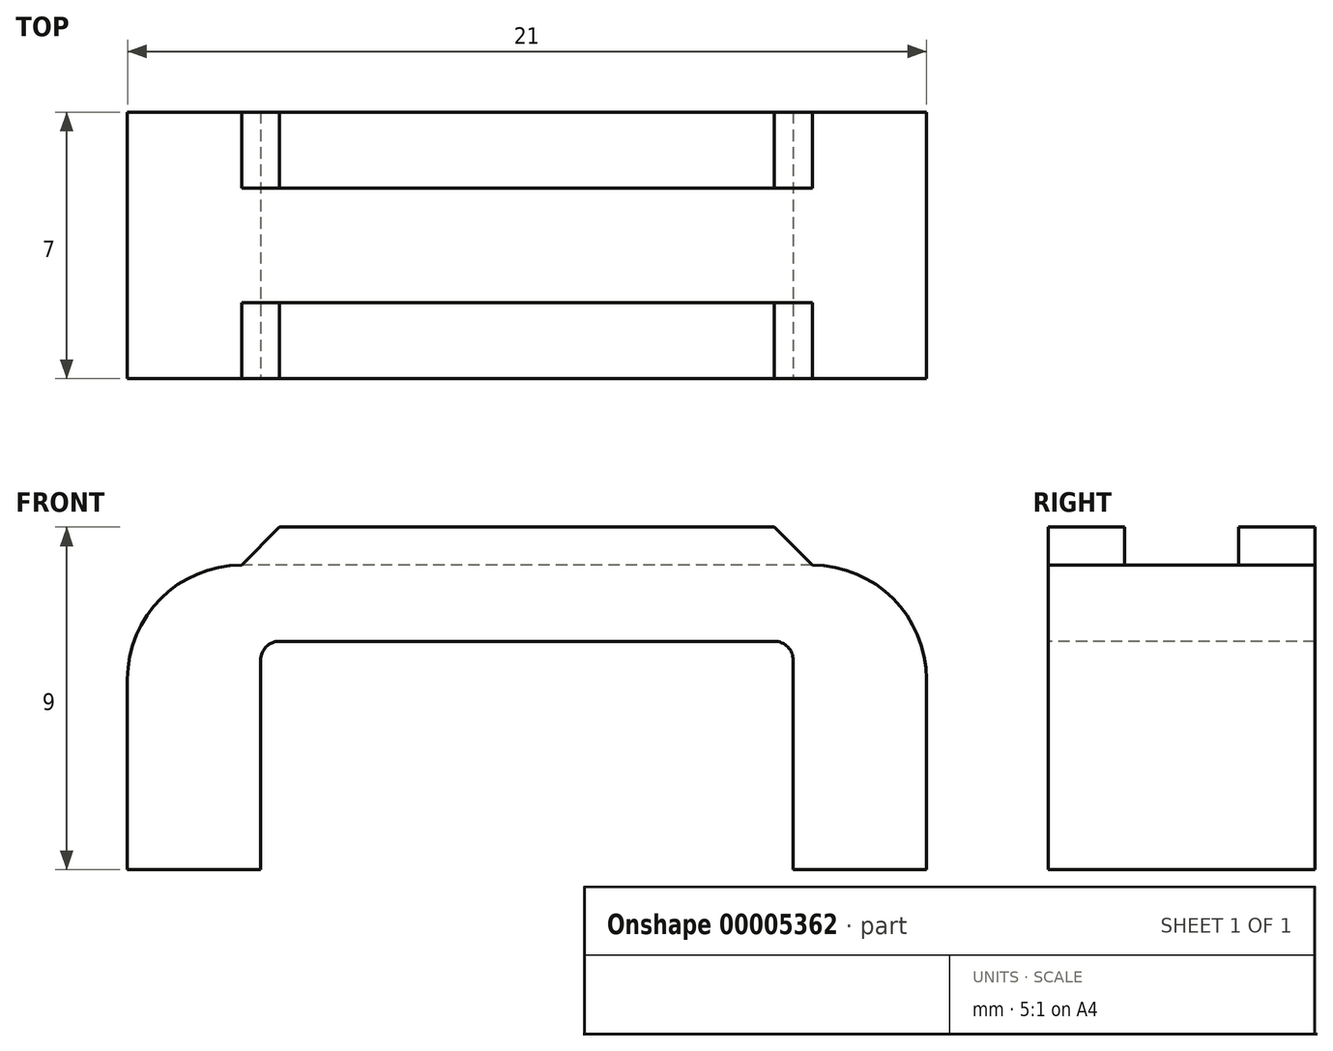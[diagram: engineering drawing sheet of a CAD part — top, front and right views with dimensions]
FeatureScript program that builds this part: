
annotation { "Feature Type Name" : "Feature", "Feature Type Description" : "" }
export const myFeature = defineFeature(function(context is Context, id is Id, definition is map)
    precondition{}
    {
        {
            var Q0;
            Q0=qCreatedBy(makeId("Top.planeOp"),FACE);
            var sketch = newSketch(context, id + "F0", { "sketchPlane" : qUnion([Q0])});
            skLineSegment(sketch, "E0.bottom", {"start": v(-26.45, 12.14) * mm, "end": v(-5.45, 12.14) * mm});
            skLineSegment(sketch, "E0.top", {"start": v(-26.45, 5.14) * mm, "end": v(-5.45, 5.14) * mm});
            skLineSegment(sketch, "E0.left", {"start": v(-26.45, 12.14) * mm, "end": v(-26.45, 5.14) * mm});
            skLineSegment(sketch, "E0.right", {"start": v(-5.45, 12.14) * mm, "end": v(-5.45, 5.14) * mm});
            skSolve(sketch);
        }
        {
            var Q0;
            Q0 = qSketchRegion(id + "F0", true);
            extrude(context, id + "F1", {"entities" : qUnion([Q0]), "depth" : 8 * mm});
        }
        {
            var Q0;
            Q0=makeQuery(id+"F1.opExtrude","SWEPT_FACE",FACE,{"disambiguationData":[OSD([sQuery(id+"F0.wireOp",EDGE,"E0.top")])]});
            var sketch = newSketch(context, id + "F2", { "sketchPlane" : qUnion([Q0])});
            skLineSegment(sketch, "E1.bottom", {"start": v(-22.95, 0) * mm, "end": v(-8.95, 0) * mm});
            skLineSegment(sketch, "E1.top", {"start": v(-22.95, 6) * mm, "end": v(-8.95, 6) * mm});
            skLineSegment(sketch, "E1.left", {"start": v(-22.95, 0) * mm, "end": v(-22.95, 6) * mm});
            skLineSegment(sketch, "E1.right", {"start": v(-8.95, 0) * mm, "end": v(-8.95, 6) * mm});
            skSolve(sketch);
        }
        {
            var Q0;
            Q0=makeQuery(id+"F2.imprint","IMPRINT",FACE,{"disambiguationData":[TD([[makeQuery(id+"F2.imprint","IMPRINT",EDGE,{"derivedFrom":sQuery(id+"F2.wireOp",EDGE,"E1.bottom")}),1.0]])]});
            extrude(context, id + "F3", {"entities" : qUnion([Q0]), "operationType" : NewBodyOperationType.REMOVE, "oppositeDirection" : true, "depth" : 25 * mm});
        }
        {
            var Q0;
            Q0=makeQuery(id+"F3.boolean.opBoolean","COPY",EDGE,{"derivedFrom":makeQuery(id+"F3.opExtrude","SWEPT_EDGE",EDGE,{"disambiguationData":[OSD([sQuery(id+"F2.wireOp",EDGE,"E1.top"),sQuery(id+"F2.wireOp",EDGE,"E1.left")])]})});
            var Q1;
            Q1=makeQuery(id+"F3.boolean.opBoolean","COPY",EDGE,{"derivedFrom":makeQuery(id+"F3.opExtrude","SWEPT_EDGE",EDGE,{"disambiguationData":[OSD([sQuery(id+"F2.wireOp",EDGE,"E1.top"),sQuery(id+"F2.wireOp",EDGE,"E1.right")])]})});
            fillet(context, id + "F4", {"entities" : qUnion([Q0, Q1]), "radius" : .5 * mm, "tangentPropagation" : true, "allowEdgeOverflow" : false});
        }
        {
            var Q0;
            Q0=makeQuery(id+"F1.opExtrude","CAP_EDGE",EDGE,{"disambiguationData":[OSD([sQuery(id+"F0.wireOp",EDGE,"E0.left")])],"isStart":false});
            var Q1;
            Q1=makeQuery(id+"F1.opExtrude","CAP_EDGE",EDGE,{"disambiguationData":[OSD([sQuery(id+"F0.wireOp",EDGE,"E0.right")])],"isStart":false});
            fillet(context, id + "F5", {"entities" : qUnion([Q0, Q1]), "radius" : 3 * mm, "tangentPropagation" : true, "allowEdgeOverflow" : false});
        }
        {
            var Q0;
            Q0=makeQuery(id+"F1.opExtrude","CAP_FACE",FACE,{"disambiguationData":[OSD([sQuery(id+"F0.wireOp",EDGE,"E0.bottom"),sQuery(id+"F0.wireOp",EDGE,"E0.top"),sQuery(id+"F0.wireOp",EDGE,"E0.left"),sQuery(id+"F0.wireOp",EDGE,"E0.right")])],"isStart":false});
            var sketch = newSketch(context, id + "F6", { "sketchPlane" : qUnion([Q0])});
            skLineSegment(sketch, "E2.bottom", {"start": v(-23.45, 12.14) * mm, "end": v(-8.45, 12.14) * mm});
            skLineSegment(sketch, "E2.top", {"start": v(-23.45, 10.14) * mm, "end": v(-8.45, 10.14) * mm});
            skLineSegment(sketch, "E2.left", {"start": v(-23.45, 12.14) * mm, "end": v(-23.45, 10.14) * mm});
            skLineSegment(sketch, "E2.right", {"start": v(-8.45, 12.14) * mm, "end": v(-8.45, 10.14) * mm});
            skLineSegment(sketch, "E3.bottom", {"start": v(-8.45, 5.14) * mm, "end": v(-23.45, 5.14) * mm});
            skLineSegment(sketch, "E3.top", {"start": v(-8.45, 7.14) * mm, "end": v(-23.45, 7.14) * mm});
            skLineSegment(sketch, "E3.left", {"start": v(-8.45, 5.14) * mm, "end": v(-8.45, 7.14) * mm});
            skLineSegment(sketch, "E3.right", {"start": v(-23.45, 5.14) * mm, "end": v(-23.45, 7.14) * mm});
            skSolve(sketch);
        }
        {
            var Q0;
            Q0 = qSketchRegion(id + "F6", true);
            extrude(context, id + "F7", {"entities" : qUnion([Q0]), "operationType" : NewBodyOperationType.ADD, "depth" : 1 * mm});
        }
        {
            var Q0;
            Q0=makeQuery(id+"F7.opExtrude","CAP_EDGE",EDGE,{"disambiguationData":[OSD([sQuery(id+"F6.wireOp",EDGE,"E3.right")])],"isStart":false});
            var Q1;
            Q1=makeQuery(id+"F7.opExtrude","CAP_EDGE",EDGE,{"disambiguationData":[OSD([sQuery(id+"F6.wireOp",EDGE,"E2.left")])],"isStart":false});
            var Q2;
            Q2=makeQuery(id+"F7.opExtrude","CAP_EDGE",EDGE,{"disambiguationData":[OSD([sQuery(id+"F6.wireOp",EDGE,"E3.left")])],"isStart":false});
            var Q3;
            Q3=makeQuery(id+"F7.opExtrude","CAP_EDGE",EDGE,{"disambiguationData":[OSD([sQuery(id+"F6.wireOp",EDGE,"E2.right")])],"isStart":false});
            chamfer(context, id + "F8", {"entities" : qUnion([Q0, Q1, Q2, Q3]), "width" : 1 * mm, "tangentPropagation" : true});
        }
    });
